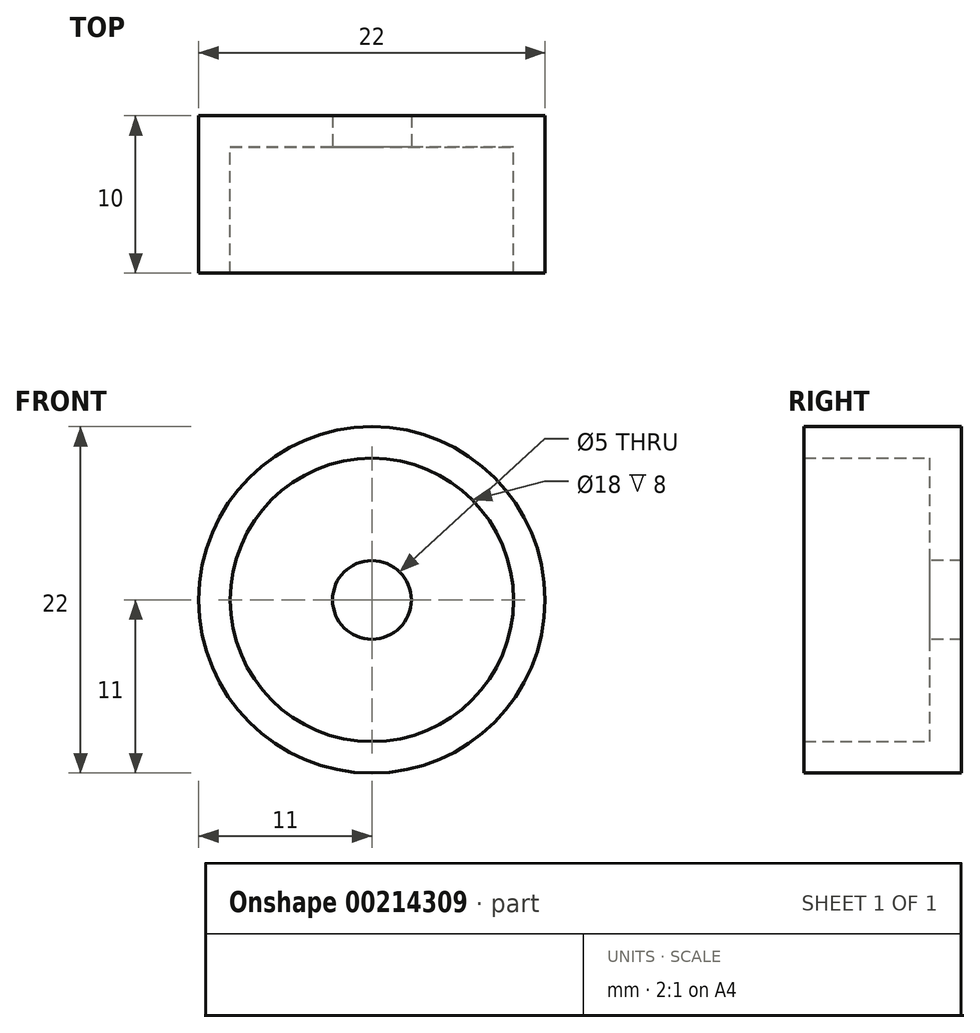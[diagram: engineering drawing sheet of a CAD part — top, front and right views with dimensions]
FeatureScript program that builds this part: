
annotation { "Feature Type Name" : "Feature", "Feature Type Description" : "" }
export const myFeature = defineFeature(function(context is Context, id is Id, definition is map)
    precondition{}
    {
        {
            var Q0;
            Q0=qCreatedBy(makeId("Front.planeOp"),FACE);
            var sketch = newSketch(context, id + "F0", { "sketchPlane" : qUnion([Q0])});
            skCircle(sketch, "E0", {"center": v(0, 0) * mm, "radius": 11 * mm});
            skSolve(sketch);
        }
        {
            var Q0;
            Q0 = qSketchRegion(id + "F0", true);
            extrude(context, id + "F1", {"entities" : qUnion([Q0]), "depth" : 2 * mm});
        }
        {
            var Q0;
            Q0=makeQuery(id+"F1.opExtrude","CAP_FACE",FACE,{"disambiguationData":[OSD([sQuery(id+"F0.wireOp",EDGE,"E0")])],"isStart":false});
            var sketch = newSketch(context, id + "F2", { "sketchPlane" : qUnion([Q0])});
            skCircle(sketch, "E1", {"center": v(0, 0) * mm, "radius": 2.5 * mm});
            skSolve(sketch);
        }
        {
            var Q0;
            Q0 = qSketchRegion(id + "F2", true);
            extrude(context, id + "F3", {"entities" : qUnion([Q0]), "operationType" : NewBodyOperationType.REMOVE, "oppositeDirection" : true, "depth" : 25 * mm});
        }
        {
            var Q0;
            Q0=makeQuery(id+"F1.opExtrude","CAP_FACE",FACE,{"disambiguationData":[OSD([sQuery(id+"F0.wireOp",EDGE,"E0")])],"isStart":false});
            var sketch = newSketch(context, id + "F4", { "sketchPlane" : qUnion([Q0])});
            skCircle(sketch, "E2", {"center": v(0, 0) * mm, "radius": 11 * mm});
            skCircle(sketch, "E3", {"center": v(0, 0) * mm, "radius": 9 * mm});
            skSolve(sketch);
        }
        {
            var Q0;
            Q0 = qSketchRegion(id + "F4", true);
            extrude(context, id + "F5", {"entities" : qUnion([Q0]), "operationType" : NewBodyOperationType.ADD, "depth" : 8 * mm});
        }
    });
